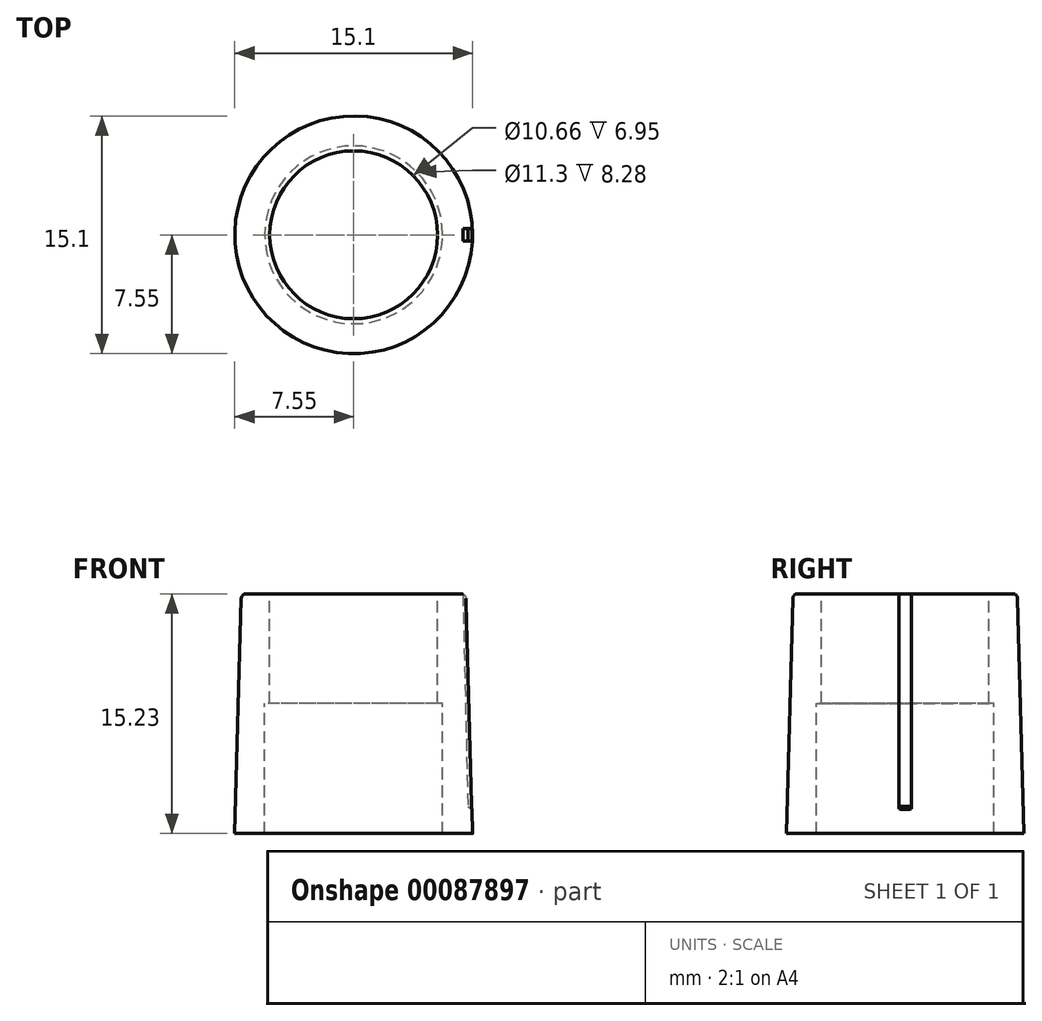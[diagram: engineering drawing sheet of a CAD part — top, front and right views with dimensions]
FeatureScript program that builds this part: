
annotation { "Feature Type Name" : "Feature", "Feature Type Description" : "" }
export const myFeature = defineFeature(function(context is Context, id is Id, definition is map)
    precondition{}
    {
        {
            var Q0;
            Q0=qCreatedBy(makeId("Front.planeOp"),FACE);
            var sketch = newSketch(context, id + "F0", { "sketchPlane" : qUnion([Q0])});
            skLineSegment(sketch, "E0", {"start": v(0, 15.38) * mm, "end": v(0, 0) * mm, "construction": true});
            skLineSegment(sketch, "E1", {"start": v(-5.33, 8.28) * mm, "end": v(-5.65, 8.28) * mm});
            skLineSegment(sketch, "E2", {"start": v(-5.65, 8.28) * mm, "end": v(-5.65, 0) * mm});
            skLineSegment(sketch, "E3", {"start": v(-5.65, 0) * mm, "end": v(-7.55, 0) * mm});
            skLineSegment(sketch, "E4", {"start": v(-7.55, 0) * mm, "end": v(-7.14, 14.94) * mm});
            skLineSegment(sketch, "E5", {"start": v(-5.33, 15.23) * mm, "end": v(-5.33, 8.28) * mm});
            skLineSegment(sketch, "E6", {"start": v(-6.84, 15.23) * mm, "end": v(-5.33, 15.23) * mm});
            skPoint(sketch, "E7.visualSharp", {"position": v(-7.13, 15.23) * mm});
            skArc(sketch, "E7.filletArc", {"start": v(-6.84, 15.23) * mm, "mid": v(-7.05, 15.15) * mm, "end": v(-7.14, 14.94) * mm});
            skSolve(sketch);
        }
        {
            var Q0;
            Q0=makeQuery(id+"F0.imprint","IMPRINT",FACE,{"disambiguationData":[TD([[makeQuery(id+"F0.imprint","IMPRINT",EDGE,{"derivedFrom":sQuery(id+"F0.wireOp",EDGE,"E1")}),-1.0]])]});
            var Q1;
            Q1=sQuery(id+"F0.wireOp",EDGE,"E0");
            revolve(context, id + "F1", {"entities" : qUnion([Q0]), "axis" : qUnion([Q1]), "revolveType" : RevolveType.FULL});
        }
        {
            var Q0;
            Q0=qCreatedBy(makeId("Front.planeOp"),FACE);
            var sketch = newSketch(context, id + "F2", { "sketchPlane" : qUnion([Q0])});
            skLineSegment(sketch, "E8", {"start": v(6.94, 15.23) * mm, "end": v(7.25, 1.73) * mm});
            skLineSegment(sketch, "E9", {"start": v(7.25, 1.73) * mm, "end": v(9.36, 0.18) * mm});
            skLineSegment(sketch, "E10", {"start": v(9.36, 0.18) * mm, "end": v(9.36, 15.26) * mm});
            skLineSegment(sketch, "E11", {"start": v(9.36, 15.26) * mm, "end": v(6.94, 15.23) * mm});
            skSolve(sketch);
        }
        {
            var Q0;
            Q0=makeQuery(id+"F2.imprint","IMPRINT",FACE,{"disambiguationData":[TD([[makeQuery(id+"F2.imprint","IMPRINT",EDGE,{"derivedFrom":sQuery(id+"F2.wireOp",EDGE,"E8")}),1.0]])]});
            extrude(context, id + "F3", {"entities" : qUnion([Q0]), "operationType" : NewBodyOperationType.REMOVE, "endBound" : BoundingType.SYMMETRIC, "oppositeDirection" : true, "depth" : .8 * mm});
        }
    });
